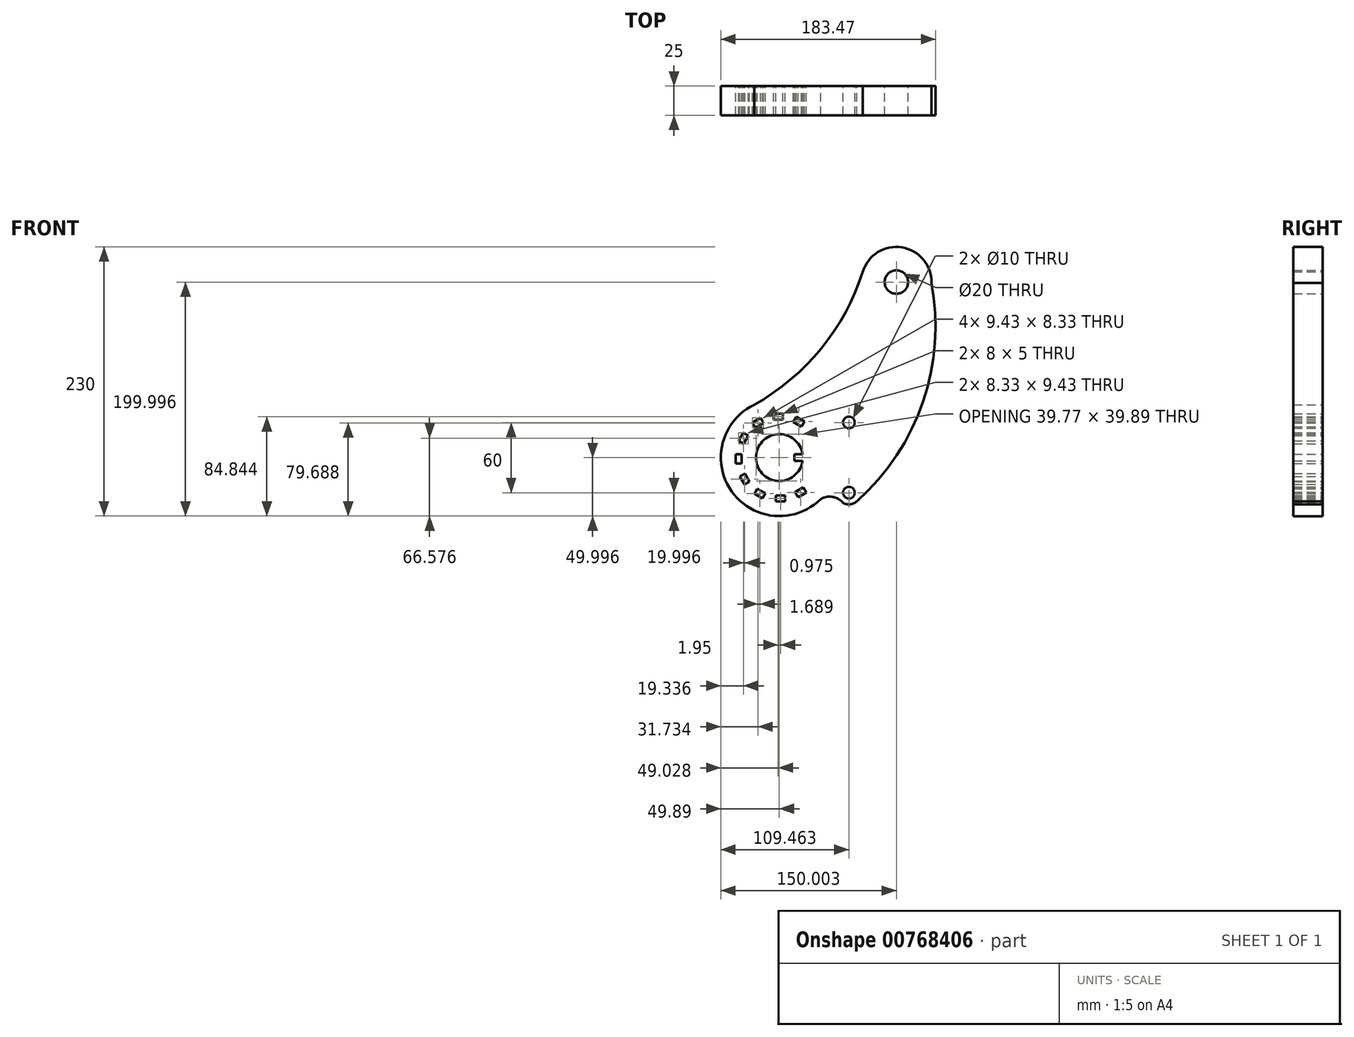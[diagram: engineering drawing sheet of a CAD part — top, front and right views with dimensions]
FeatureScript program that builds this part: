
annotation { "Feature Type Name" : "Feature", "Feature Type Description" : "" }
export const myFeature = defineFeature(function(context is Context, id is Id, definition is map)
    precondition{}
    {
        {
            var Q0;
            Q0=qCreatedBy(makeId("Front.planeOp"),FACE);
            var sketch = newSketch(context, id + "F0", { "sketchPlane" : qUnion([Q0])});
            skCircle(sketch, "E0", {"center": v(30.98, 97.07) * mm, "radius": 10 * mm});
            skCircle(sketch, "E1", {"center": v(30.98, 97.07) * mm, "radius": 30 * mm});
            skArc(sketch, "E2", {"start": v(-33.78, -17.46) * mm, "mid": v(-119.02, -52.93) * mm, "end": v(-33.78, -88.4) * mm});
            skLineSegment(sketch, "E3", {"start": v(-69.02, -52.93) * mm, "end": v(11.22, -52.93) * mm, "construction": true});
            skCircle(sketch, "E4", {"center": v(-9.56, -82.93) * mm, "radius": 5 * mm});
            skCircle(sketch, "E5.MirrorC", {"center": v(-9.56, -22.93) * mm, "radius": 5 * mm});
            skArc(sketch, "E6", {"start": v(-7.48, -32.72) * mm, "mid": v(-0.25, -19.28) * mm, "end": v(-14.69, -14.35) * mm});
            skArc(sketch, "E7", {"start": v(-14.69, -91.52) * mm, "mid": v(-0.25, -86.59) * mm, "end": v(-7.48, -73.15) * mm});
            skArc(sketch, "E8.MirrorC", {"start": v(-7.48, -73.15) * mm, "mid": v(-0.25, -86.59) * mm, "end": v(-14.69, -91.52) * mm});
            skLineSegment(sketch, "E9", {"start": v(-49.24, -49.93) * mm, "end": v(-56.24, -49.93) * mm});
            skLineSegment(sketch, "E10", {"start": v(-56.24, -49.93) * mm, "end": v(-56.24, -55.93) * mm});
            skLineSegment(sketch, "E11", {"start": v(-56.24, -55.93) * mm, "end": v(-49.24, -55.93) * mm});
            skArc(sketch, "E12", {"start": v(-33.78, -17.46) * mm, "mid": v(-23.66, -19.4) * mm, "end": v(-14.69, -14.35) * mm});
            skArc(sketch, "E13.MirrorCS", {"start": v(-33.78, -88.4) * mm, "mid": v(-23.66, -86.47) * mm, "end": v(-14.69, -91.52) * mm});
            skArc(sketch, "E14", {"start": v(-25.57, -40.93) * mm, "mid": v(-34.05, -44.45) * mm, "end": v(-37.57, -52.93) * mm});
            skArc(sketch, "E15.MirrorCS", {"start": v(-25.57, -64.93) * mm, "mid": v(-34.05, -61.42) * mm, "end": v(-37.57, -52.93) * mm});
            skArc(sketch, "E16", {"start": v(-25.57, -40.93) * mm, "mid": v(-14.97, -40.25) * mm, "end": v(-7.48, -32.72) * mm});
            skArc(sketch, "E17.MirrorCS", {"start": v(-25.57, -64.93) * mm, "mid": v(-14.97, -65.62) * mm, "end": v(-7.48, -73.15) * mm});
            skArc(sketch, "E18", {"start": v(-95.18, -10.32) * mm, "mid": v(-34.79, 38.42) * mm, "end": v(2.5, 106.5) * mm});
            skArc(sketch, "E19", {"start": v(-3.12, -90.6) * mm, "mid": v(53.64, -5.57) * mm, "end": v(60.98, 96.4) * mm});
            skArc(sketch, "E20", {"start": v(-49.24, -49.93) * mm, "mid": v(-89.02, -52.93) * mm, "end": v(-49.24, -55.93) * mm});
            skPoint(sketch, "E21.center", {"position": v(0, 0) * mm});
            skLineSegment(sketch, "E22.bottom", {"start": v(-74, -15.59) * mm, "end": v(-66, -15.59) * mm});
            skLineSegment(sketch, "E22.top", {"start": v(-74, -20.59) * mm, "end": v(-66, -20.59) * mm});
            skLineSegment(sketch, "E22.left", {"start": v(-74, -15.59) * mm, "end": v(-74, -20.59) * mm});
            skLineSegment(sketch, "E22.right", {"start": v(-66, -15.59) * mm, "end": v(-66, -20.59) * mm});
            skLineSegment(sketch, "E23.1.0", {"start": v(50.5, -56.29) * mm, "end": v(46.5, -49.36) * mm});
            skLineSegment(sketch, "E23.2.0", {"start": v(23.5, 71.87) * mm, "end": v(19.5, 64.94) * mm});
            skLineSegment(sketch, "E24.1.0", {"start": v(-54.65, -18.1) * mm, "end": v(-47.72, -22.1) * mm});
            skLineSegment(sketch, "E24.1.1", {"start": v(-47.72, -22.1) * mm, "end": v(-50.22, -26.43) * mm});
            skLineSegment(sketch, "E24.1.2", {"start": v(-57.15, -22.43) * mm, "end": v(-50.22, -26.43) * mm});
            skLineSegment(sketch, "E24.1.3", {"start": v(-54.65, -18.1) * mm, "end": v(-57.15, -22.43) * mm});
            skLineSegment(sketch, "E24.5.0", {"start": v(-46.03, -82.8) * mm, "end": v(-52.96, -86.8) * mm});
            skLineSegment(sketch, "E24.5.1", {"start": v(-52.96, -86.8) * mm, "end": v(-55.46, -82.46) * mm});
            skLineSegment(sketch, "E24.5.2", {"start": v(-48.53, -78.46) * mm, "end": v(-55.46, -82.46) * mm});
            skLineSegment(sketch, "E24.5.3", {"start": v(-46.03, -82.8) * mm, "end": v(-48.53, -78.46) * mm});
            skLineSegment(sketch, "E24.6.0", {"start": v(-64.04, -90.28) * mm, "end": v(-72.04, -90.28) * mm});
            skLineSegment(sketch, "E24.6.1", {"start": v(-72.04, -90.28) * mm, "end": v(-72.04, -85.28) * mm});
            skLineSegment(sketch, "E24.6.2", {"start": v(-64.04, -85.28) * mm, "end": v(-72.04, -85.28) * mm});
            skLineSegment(sketch, "E24.6.3", {"start": v(-64.04, -90.28) * mm, "end": v(-64.04, -85.28) * mm});
            skLineSegment(sketch, "E24.7.0", {"start": v(-83.38, -87.77) * mm, "end": v(-90.31, -83.77) * mm});
            skLineSegment(sketch, "E24.7.1", {"start": v(-90.31, -83.77) * mm, "end": v(-87.81, -79.44) * mm});
            skLineSegment(sketch, "E24.7.2", {"start": v(-80.88, -83.44) * mm, "end": v(-87.81, -79.44) * mm});
            skLineSegment(sketch, "E24.7.3", {"start": v(-83.38, -87.77) * mm, "end": v(-80.88, -83.44) * mm});
            skLineSegment(sketch, "E24.8.0", {"start": v(-98.87, -75.92) * mm, "end": v(-102.87, -68.99) * mm});
            skLineSegment(sketch, "E24.8.1", {"start": v(-102.87, -68.99) * mm, "end": v(-98.54, -66.49) * mm});
            skLineSegment(sketch, "E24.8.2", {"start": v(-94.54, -73.42) * mm, "end": v(-98.54, -66.49) * mm});
            skLineSegment(sketch, "E24.8.3", {"start": v(-98.87, -75.92) * mm, "end": v(-94.54, -73.42) * mm});
            skLineSegment(sketch, "E24.9.0", {"start": v(-106.37, -57.9) * mm, "end": v(-106.37, -49.9) * mm});
            skLineSegment(sketch, "E24.9.1", {"start": v(-106.37, -49.9) * mm, "end": v(-101.37, -49.9) * mm});
            skLineSegment(sketch, "E24.9.2", {"start": v(-101.37, -57.9) * mm, "end": v(-101.37, -49.9) * mm});
            skLineSegment(sketch, "E24.9.3", {"start": v(-106.37, -57.9) * mm, "end": v(-101.37, -57.9) * mm});
            skLineSegment(sketch, "E24.10.0", {"start": v(-103.85, -38.57) * mm, "end": v(-99.85, -31.64) * mm});
            skLineSegment(sketch, "E24.10.1", {"start": v(-99.85, -31.64) * mm, "end": v(-95.52, -34.14) * mm});
            skLineSegment(sketch, "E24.10.2", {"start": v(-99.52, -41.07) * mm, "end": v(-95.52, -34.14) * mm});
            skLineSegment(sketch, "E24.10.3", {"start": v(-103.85, -38.57) * mm, "end": v(-99.52, -41.07) * mm});
            skLineSegment(sketch, "E24.11.0", {"start": v(-92, -23.08) * mm, "end": v(-85.07, -19.08) * mm});
            skLineSegment(sketch, "E24.11.1", {"start": v(-85.07, -19.08) * mm, "end": v(-82.57, -23.4) * mm});
            skLineSegment(sketch, "E24.11.2", {"start": v(-89.5, -27.4) * mm, "end": v(-82.57, -23.4) * mm});
            skLineSegment(sketch, "E24.11.3", {"start": v(-92, -23.08) * mm, "end": v(-89.5, -27.4) * mm});
            skLineSegment(sketch, "E24.anchor1", {"start": v(-69.02, -52.93) * mm, "end": v(-74, -15.59) * mm, "construction": true});
            skLineSegment(sketch, "E24.anchor2", {"start": v(-69.02, -52.93) * mm, "end": v(-92, -23.08) * mm, "construction": true});
            skSolve(sketch);
        }
        {
            var Q0;
            Q0 = qSketchRegion(id + "F0", true);
            extrude(context, id + "F1", {"entities" : qUnion([Q0]), "depth" : 25 * mm, "offsetDistance" : 25 * mm});
        }
    });
